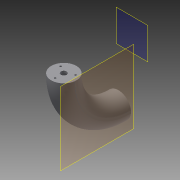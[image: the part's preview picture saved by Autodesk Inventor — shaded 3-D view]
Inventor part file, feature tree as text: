
AUTODESK INVENTOR PART (.ipt)
format: ipt  version: 2014 (Build 180170000, 170)  size: 297,472 bytes
history: native  units: mm
features: sketch x9, extrude x7, other x3, fillet x2, sweep x1, shell x1
ambient origin geometry x8: Origin, YZ Plane, XZ Plane, XY Plane, X Axis, Y Axis, Z Axis, Center Point
bodies: Body1 (feature_tree)
feature tree (23):
  other  "ソリッド1"
  sketch  "スケッチ1"
  other  "作業平面1"
  sweep  "スイープ1"
  extrude  "押し出し1"  Depth=95.0mm
  shell  "シェル1"  Thickness=0.0mm
  extrude  "押し出し2"  TaperAngle=0.0deg  [1 undecoded]
  extrude  "押し出し3"  Depth=75.0mm
  extrude  "押し出し4"  TaperAngle=0.0deg  [1 undecoded]
  fillet  "フィレット2"  Radius=8.0mm
  other  "作業平面2"
  extrude  "押し出し5"  Depth=2.6mm
  extrude  "押し出し6"  Depth=12.0mm
  extrude  "押し出し7"  TaperAngle=0.0deg  [1 undecoded]
  fillet  "フィレット3"  Radius=30.0mm
  sketch  "スケッチ3"
  sketch  "スケッチ4"
  sketch  "スケッチ5"
  sketch  "スケッチ6"
  sketch  "スケッチ7"
  sketch  "スケッチ8"
  sketch  "スケッチ9"
  sketch  "スケッチ10"
note: 3 required parameter values undecoded (feature->parameter linkage not recoverable at this tier; creation-order binding heuristic only, values carry confidence <= 0.55)
